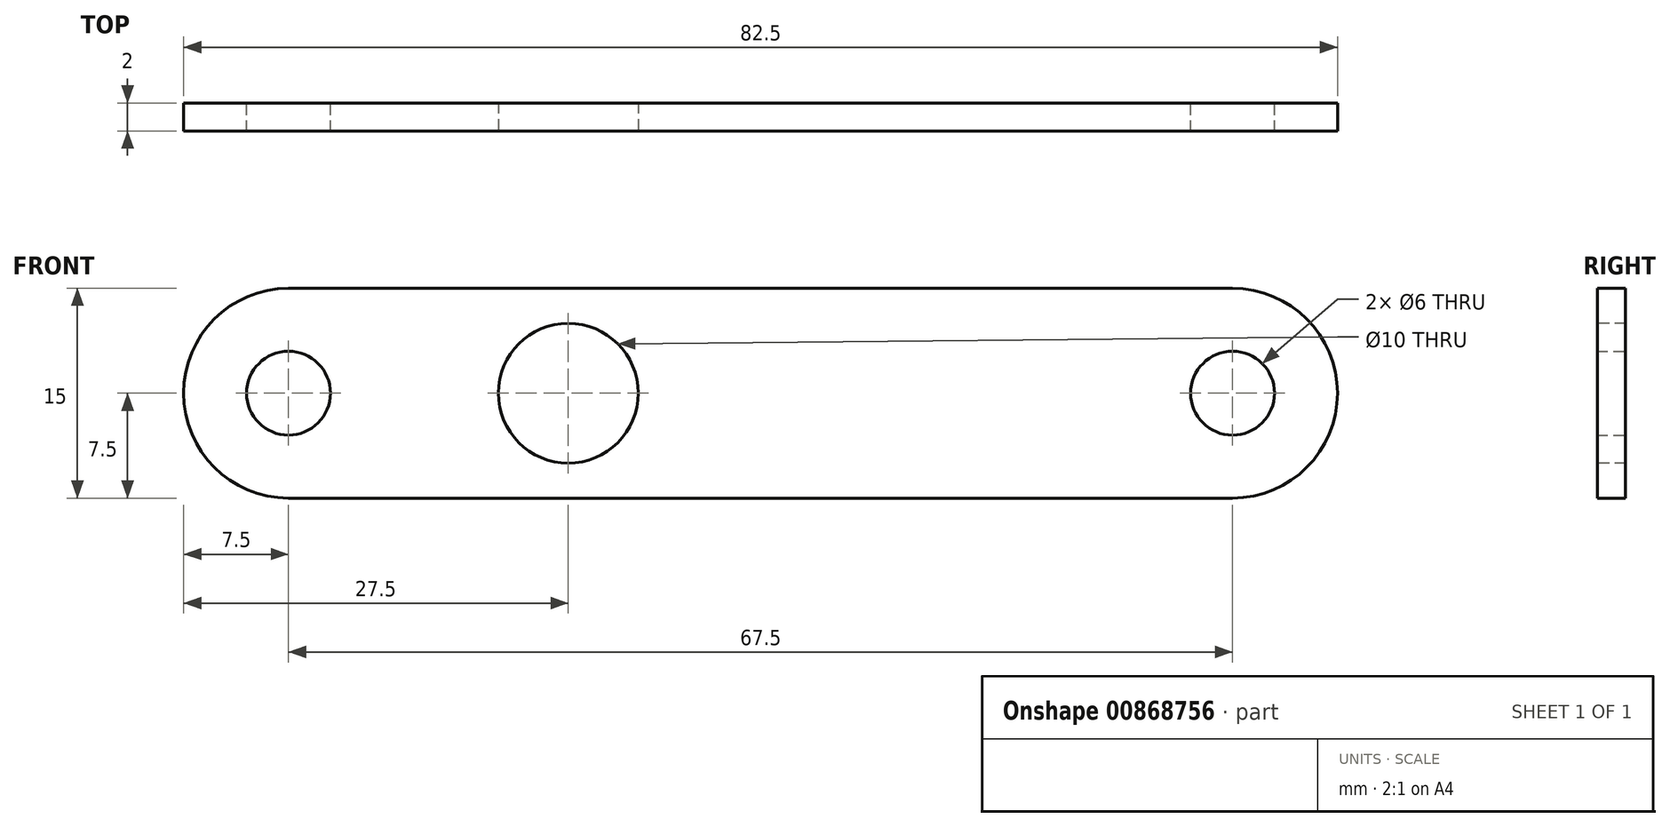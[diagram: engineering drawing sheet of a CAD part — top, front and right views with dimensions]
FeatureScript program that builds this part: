
annotation { "Feature Type Name" : "Feature", "Feature Type Description" : "" }
export const myFeature = defineFeature(function(context is Context, id is Id, definition is map)
    precondition{}
    {
        {
            var Q0;
            Q0=qCreatedBy(makeId("Front.planeOp"),FACE);
            var sketch = newSketch(context, id + "F0", { "sketchPlane" : qUnion([Q0])});
            skCircle(sketch, "E0", {"center": v(0, 0) * mm, "radius": 3 * mm});
            skLineSegment(sketch, "E1.bottom", {"start": v(-7.5, -7.5) * mm, "end": v(75, -7.5) * mm});
            skLineSegment(sketch, "E1.top", {"start": v(-7.5, 7.5) * mm, "end": v(75, 7.5) * mm});
            skLineSegment(sketch, "E1.left", {"start": v(-7.5, -7.5) * mm, "end": v(-7.5, 7.5) * mm});
            skLineSegment(sketch, "E1.right", {"start": v(75, -7.5) * mm, "end": v(75, 7.5) * mm});
            skCircle(sketch, "E2", {"center": v(135, 0) * mm, "radius": 3 * mm, "construction": true});
            skCircle(sketch, "E3", {"center": v(67.5, 0) * mm, "radius": 3 * mm});
            skSolve(sketch);
        }
        {
            var Q0;
            Q0=makeQuery(id+"F0.imprint","IMPRINT",FACE,{"disambiguationData":[TD([[makeQuery(id+"F0.imprint","IMPRINT",EDGE,{"derivedFrom":sQuery(id+"F0.wireOp",EDGE,"E0")}),-1.0]])]});
            extrude(context, id + "F1", {"entities" : qUnion([Q0]), "depth" : 2 * mm, "offsetDistance" : 25 * mm, "symmetric" : true});
        }
        {
            var Q0;
            Q0=makeQuery(id+"F1.opExtrude","SWEPT_EDGE",EDGE,{"disambiguationData":[OSD([sQuery(id+"F0.wireOp",EDGE,"E1.top"),sQuery(id+"F0.wireOp",EDGE,"E1.right")])]});
            var Q1;
            Q1=makeQuery(id+"F1.opExtrude","SWEPT_EDGE",EDGE,{"disambiguationData":[OSD([sQuery(id+"F0.wireOp",EDGE,"E1.bottom"),sQuery(id+"F0.wireOp",EDGE,"E1.right")])]});
            var Q2;
            Q2=makeQuery(id+"F1.opExtrude","SWEPT_EDGE",EDGE,{"disambiguationData":[OSD([sQuery(id+"F0.wireOp",EDGE,"E1.top"),sQuery(id+"F0.wireOp",EDGE,"E1.left")])]});
            var Q3;
            Q3=makeQuery(id+"F1.opExtrude","SWEPT_EDGE",EDGE,{"disambiguationData":[OSD([sQuery(id+"F0.wireOp",EDGE,"E1.bottom"),sQuery(id+"F0.wireOp",EDGE,"E1.left")])]});
            fillet(context, id + "F2", {"entities" : qUnion([Q0, Q1, Q2, Q3]), "radius" : 7.5 * mm, "tangentPropagation" : true, "allowEdgeOverflow" : false});
        }
        {
            var Q0;
            Q0=qCreatedBy(makeId("Front.planeOp"),FACE);
            var sketch = newSketch(context, id + "F3", { "sketchPlane" : qUnion([Q0])});
            skCircle(sketch, "E4", {"center": v(20, 0) * mm, "radius": 5 * mm});
            skSolve(sketch);
        }
        {
            var Q0;
            Q0 = qSketchRegion(id + "F3", true);
            extrude(context, id + "F4", {"entities" : qUnion([Q0]), "operationType" : NewBodyOperationType.REMOVE, "oppositeDirection" : true, "depth" : 25 * mm, "offsetDistance" : 25 * mm, "symmetric" : true});
        }
    });
